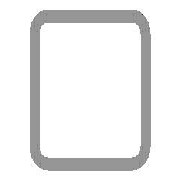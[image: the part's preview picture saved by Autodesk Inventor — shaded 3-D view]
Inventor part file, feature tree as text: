
AUTODESK INVENTOR PART (.ipt)
format: ipt  version: 2016 (Build 200138000, 138)  size: 139,776 bytes
history: native  units: mm (DEFAULTED — no unit token found)
features: other x4, sketch x3, plane x2, split x1
ambient origin geometry x8: Origin, YZ Plane, XZ Plane, XY Plane, X Axis, Y Axis, Z Axis, Center Point
bodies: Solid1 (feature_tree), Body (feature_tree)
feature tree (10):
  parser-record x1  (decoder bookkeeping rows leaked as tree rows — omitted from the tree; the rows remain in map.json)
  other  "Driven Length"
  other  "Start plane"
  other  "End plane"
  plane  "Work Plane4"
  split  "Split1"
  sketch  "Sketch"  dims[d7=4.0mm d9=25.0mm d11=25.0mm d12=2.0mm d13=0.212132mm d14=480.0mm d15=12.5mm d16=12.5mm d17=90.0deg d18=479.787868mm]
  sketch  "Sketch3"  dims[d3=479.787868mm]
  plane  "Work Plane3"
  sketch  "Sketch4"  dims[d4=0.0mm]
